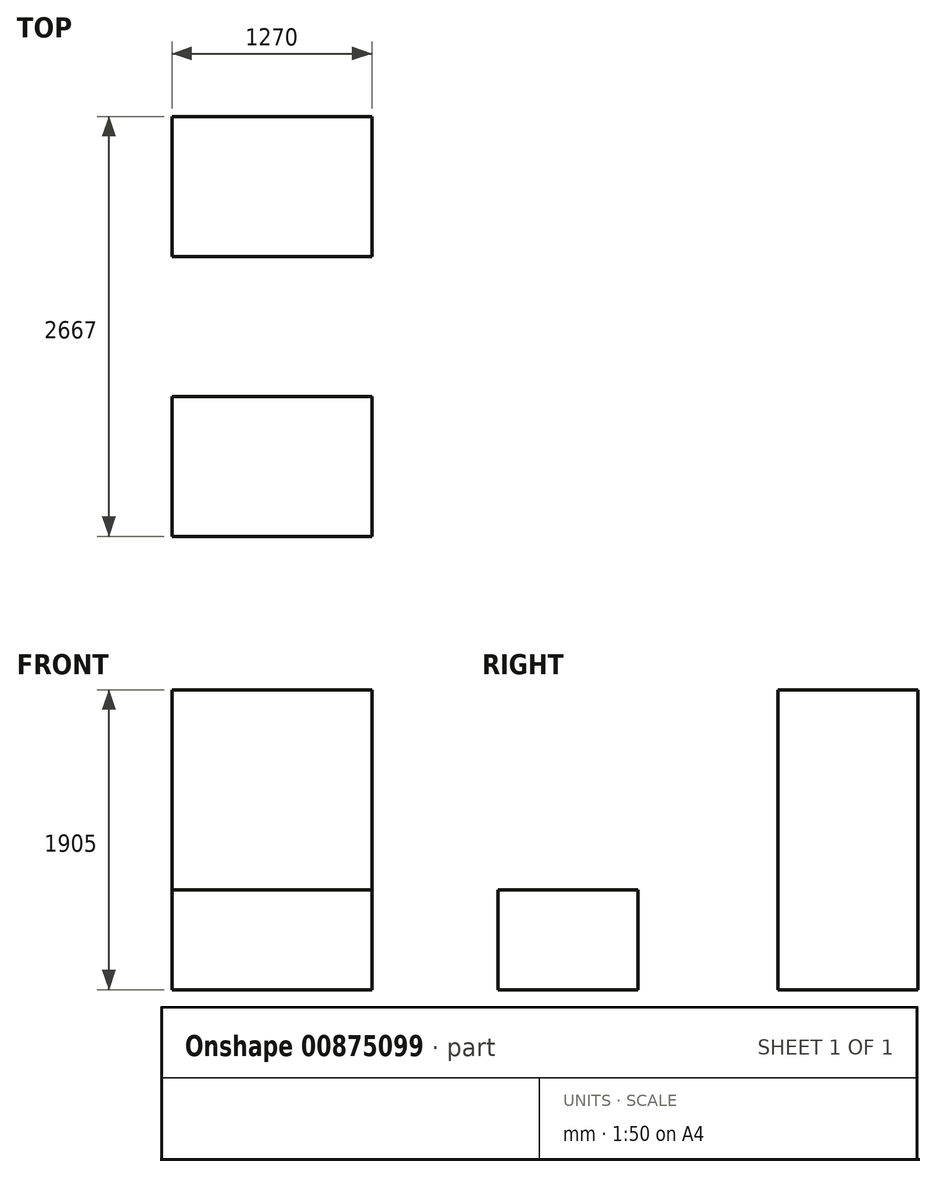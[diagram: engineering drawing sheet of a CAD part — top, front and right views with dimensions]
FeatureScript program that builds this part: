
annotation { "Feature Type Name" : "Feature", "Feature Type Description" : "" }
export const myFeature = defineFeature(function(context is Context, id is Id, definition is map)
    precondition{}
    {
        {
            var Q0;
            Q0=qCreatedBy(makeId("Top.planeOp"),FACE);
            var sketch = newSketch(context, id + "F0", { "sketchPlane" : qUnion([Q0])});
            skLineSegment(sketch, "E0", {"start": v(0, 0) * mm, "end": v(-1270, 0) * mm});
            skLineSegment(sketch, "E1", {"start": v(-1270, 0) * mm, "end": v(-1270, -2667) * mm});
            skLineSegment(sketch, "E2", {"start": v(-1270, -2667) * mm, "end": v(0, -2667) * mm});
            skLineSegment(sketch, "E3", {"start": v(0, -2667) * mm, "end": v(0, 0) * mm});
            skLineSegment(sketch, "E4", {"start": v(-1270, -2667) * mm, "end": v(-1270, -1778) * mm});
            skLineSegment(sketch, "E5", {"start": v(-1270, -1778) * mm, "end": v(0, -1778) * mm});
            skLineSegment(sketch, "E6", {"start": v(0, -1778) * mm, "end": v(0, -889) * mm});
            skLineSegment(sketch, "E7", {"start": v(0, -889) * mm, "end": v(-1270, -889) * mm});
            skLineSegment(sketch, "E8", {"start": v(-1270, -889) * mm, "end": v(-1270, 0) * mm});
            skSolve(sketch);
        }
        {
            var Q0;
            {var subQ0=sQuery(id+"F0.wireOp",EDGE,"E2");Q0=makeQuery(id+"F0.imprint","IMPRINT",FACE,{"disambiguationData":[TD([[makeQuery(id+"F0.imprint","IMPRINT",EDGE,{"derivedFrom":subQ0}),1.0]])]});}
            var sketch = newSketch(context, id + "F1", { "sketchPlane" : qUnion([Q0])});
            skSolve(sketch);
        }
        {
            var Q0;
            {var subQ0=sQuery(id+"F0.wireOp",EDGE,"E2");Q0=makeQuery(id+"F1.imprint","IMPRINT",FACE,{"disambiguationData":[TD([[makeQuery(id+"F1.imprint","IMPRINT",EDGE,{"derivedFrom":makeQuery(id+"F0.imprint","IMPRINT",EDGE,{"derivedFrom":subQ0})}),1.0]])]});}
            extrude(context, id + "F2", {"entities" : qUnion([Q0]), "depth" : 635 * mm, "offsetDistance" : 25.4 * mm});
        }
        {
            var Q0;
            Q0=makeQuery(id+"F0.imprint","IMPRINT",FACE,{"disambiguationData":[TD([[makeQuery(id+"F0.imprint","IMPRINT",EDGE,{"derivedFrom":sQuery(id+"F0.wireOp",EDGE,"E1")}),1.0]])]});
            var sketch = newSketch(context, id + "F3", { "sketchPlane" : qUnion([Q0])});
            skSolve(sketch);
        }
        {
            var Q0;
            Q0 = qSketchRegion(id + "F3", true);
            var Q1;
            Q1=makeQuery(id+"F3.imprint","IMPRINT",FACE,{"disambiguationData":[TD([[makeQuery(id+"F3.imprint","IMPRINT",EDGE,{"derivedFrom":makeQuery(id+"F0.imprint","IMPRINT",EDGE,{"derivedFrom":sQuery(id+"F0.wireOp",EDGE,"E1")})}),1.0]])]});
            extrude(context, id + "F4", {"entities" : qUnion([Q0, Q1]), "operationType" : NewBodyOperationType.ADD, "depth" : 1270 * mm, "offsetDistance" : 25.4 * mm});
        }
        {
            var Q0;
            {var subQ0=sQuery(id+"F0.wireOp",EDGE,"E0");Q0=makeQuery(id+"F0.imprint","IMPRINT",FACE,{"disambiguationData":[TD([[makeQuery(id+"F0.imprint","IMPRINT",EDGE,{"derivedFrom":subQ0}),1.0]])]});}
            var sketch = newSketch(context, id + "F5", { "sketchPlane" : qUnion([Q0])});
            skSolve(sketch);
        }
        {
            var Q0;
            Q0 = qSketchRegion(id + "F5", true);
            var Q1;
            {var subQ0=sQuery(id+"F0.wireOp",EDGE,"E0");Q1=makeQuery(id+"F0.imprint","IMPRINT",FACE,{"disambiguationData":[TD([[makeQuery(id+"F0.imprint","IMPRINT",EDGE,{"derivedFrom":subQ0}),1.0]])]});}
            extrude(context, id + "F6", {"entities" : qUnion([Q0, Q1]), "operationType" : NewBodyOperationType.ADD, "depth" : 1905 * mm, "offsetDistance" : 25.4 * mm});
        }
    });
